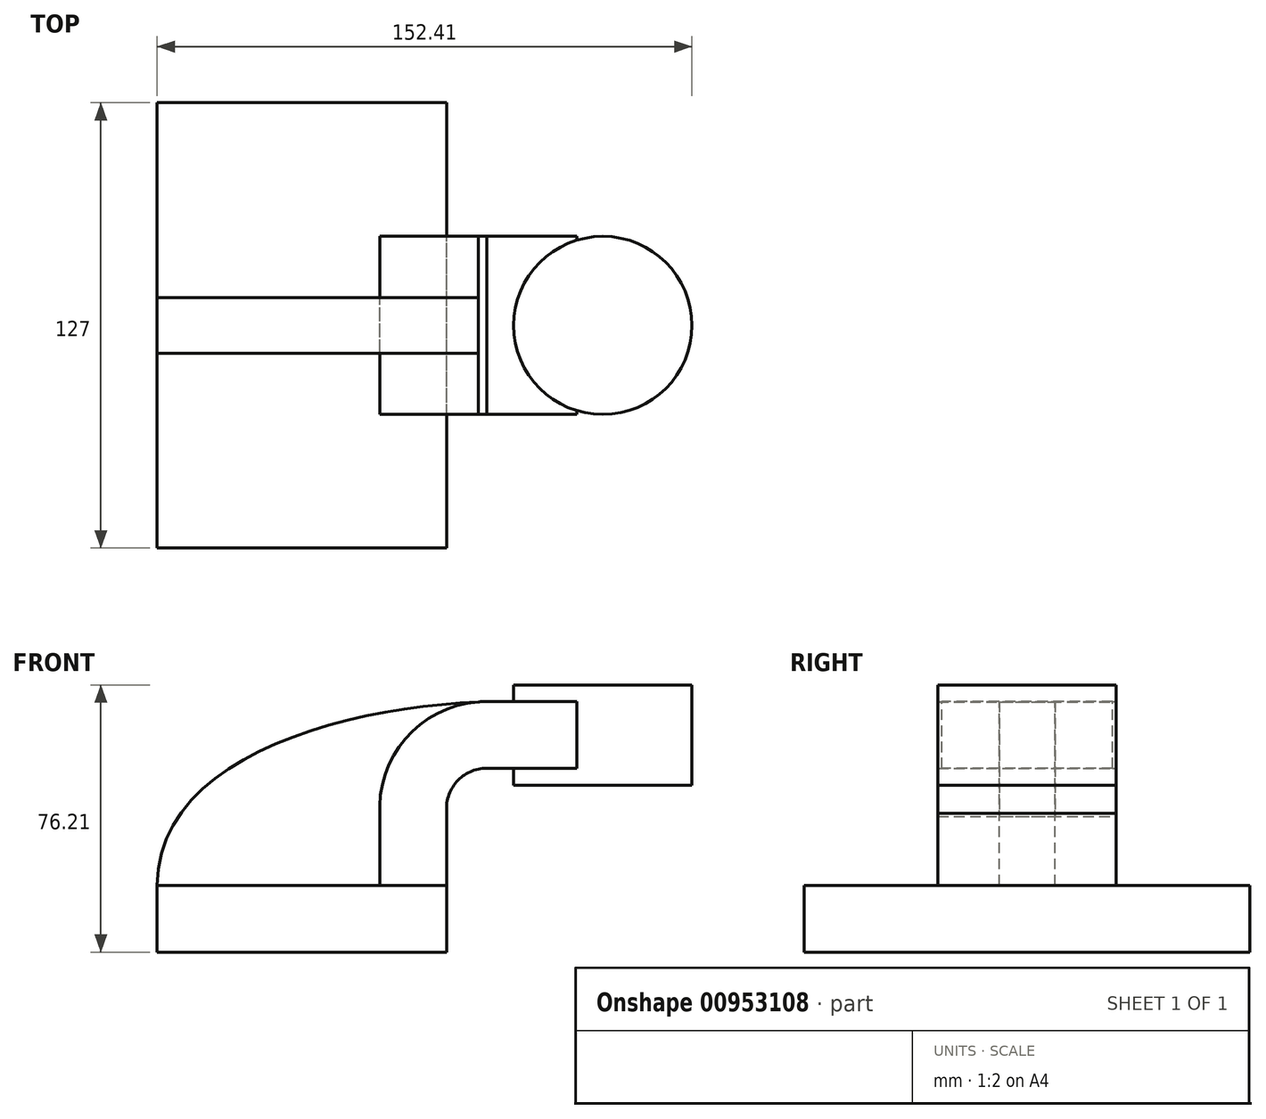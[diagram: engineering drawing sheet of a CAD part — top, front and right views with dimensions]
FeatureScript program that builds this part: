
annotation { "Feature Type Name" : "Feature", "Feature Type Description" : "" }
export const myFeature = defineFeature(function(context is Context, id is Id, definition is map)
    precondition{}
    {
        {
            var Q0;
            Q0=qCreatedBy(makeId("Front.planeOp"),FACE);
            var sketch = newSketch(context, id + "F0", { "sketchPlane" : qUnion([Q0])});
            skLineSegment(sketch, "E0.bottom", {"start": v(-41.28, -9.53) * mm, "end": v(41.28, -9.53) * mm});
            skLineSegment(sketch, "E0.top", {"start": v(-41.28, 9.52) * mm, "end": v(41.28, 9.52) * mm});
            skLineSegment(sketch, "E0.left", {"start": v(-41.28, -9.53) * mm, "end": v(-41.28, 9.53) * mm});
            skLineSegment(sketch, "E0.right", {"start": v(41.28, -9.53) * mm, "end": v(41.28, 9.52) * mm});
            skPoint(sketch, "E0.middle", {"position": v(0, 0) * mm});
            skLineSegment(sketch, "E1.bottom", {"start": v(111.12, 66.67) * mm, "end": v(60.32, 66.67) * mm});
            skLineSegment(sketch, "E1.top", {"start": v(111.12, 38.1) * mm, "end": v(60.32, 38.1) * mm});
            skLineSegment(sketch, "E1.left", {"start": v(111.12, 66.67) * mm, "end": v(111.12, 38.1) * mm});
            skLineSegment(sketch, "E1.right", {"start": v(60.32, 66.67) * mm, "end": v(60.32, 38.1) * mm});
            skPoint(sketch, "E1.middle", {"position": v(85.72, 52.39) * mm});
            skLineSegment(sketch, "E2.bottom", {"start": v(41.28, 9.52) * mm, "end": v(41.28, 9.52) * mm});
            skLineSegment(sketch, "E3", {"start": v(52.62, 42.88) * mm, "end": v(78.31, 42.88) * mm});
            skLineSegment(sketch, "E4", {"start": v(41.28, 9.52) * mm, "end": v(41.28, 30.04) * mm});
            skArc(sketch, "E5", {"start": v(52.62, 42.88) * mm, "mid": v(44.06, 39.01) * mm, "end": v(41.28, 30.04) * mm});
            skLineSegment(sketch, "E6.0", {"start": v(22.23, 9.52) * mm, "end": v(22.23, 29.15) * mm});
            skArc(sketch, "E6.1", {"start": v(52.62, 61.93) * mm, "mid": v(30.27, 52.17) * mm, "end": v(22.23, 29.15) * mm});
            skLineSegment(sketch, "E6.2", {"start": v(52.62, 61.93) * mm, "end": v(78.31, 61.93) * mm});
            skFitSpline(sketch, "E7", {"points": [v(-41.28, 9.53) * mm, v(52.62, 61.93) * mm], "startDerivative": vector(1.16, 112.53) * mm, "endDerivative": vector(116.71, 3.87) * mm});
            skLineSegment(sketch, "E8", {"start": v(78.31, 61.93) * mm, "end": v(78.31, 42.88) * mm});
            skLineSegment(sketch, "E9", {"start": v(85.72, 66.67) * mm, "end": v(85.72, 38.1) * mm});
            skSolve(sketch);
        }
        {
            var Q0;
            Q0=makeQuery(id+"F0.imprint","IMPRINT",FACE,{"disambiguationData":[TD([[makeQuery(id+"F0.imprint","IMPRINT",EDGE,{"derivedFrom":sQuery(id+"F0.wireOp",EDGE,"E0.bottom")}),1.0]])]});
            extrude(context, id + "F1", {"entities" : qUnion([Q0]), "endBound" : BoundingType.SYMMETRIC, "depth" : 127 * mm, "offsetDistance" : 25.4 * mm});
        }
        {
            var Q0;
            {var subQ6=sQuery(id+"F0.wireOp",EDGE,"E4");Q0=makeQuery(id+"F0.imprint","IMPRINT",FACE,{"disambiguationData":[TD([[makeQuery(id+"F0.imprint","IMPRINT",EDGE,{"derivedFrom":subQ6}),1.0]])]});}
            var Q1;
            {var subQ5=sQuery(id+"F0.wireOp",EDGE,"E8");Q1=makeQuery(id+"F0.imprint","IMPRINT",FACE,{"disambiguationData":[TD([[makeQuery(id+"F0.imprint","IMPRINT",EDGE,{"derivedFrom":subQ5}),-1.0]])]});}
            extrude(context, id + "F2", {"entities" : qUnion([Q0, Q1]), "endBound" : BoundingType.SYMMETRIC, "depth" : 50.8 * mm, "offsetDistance" : 25.4 * mm});
        }
        {
            var Q0;
            {var subQ3=sQuery(id+"F0.wireOp",EDGE,"E6.0");Q0=makeQuery(id+"F0.imprint","IMPRINT",FACE,{"disambiguationData":[TD([[makeQuery(id+"F0.imprint","IMPRINT",EDGE,{"derivedFrom":subQ3}),1.0]])]});}
            extrude(context, id + "F3", {"entities" : qUnion([Q0]), "endBound" : BoundingType.SYMMETRIC, "depth" : 15.88 * mm, "offsetDistance" : 25.4 * mm});
        }
        {
            var Q0;
            {var subQ0=sQuery(id+"F0.wireOp",EDGE,"E1.left");Q0=makeQuery(id+"F0.imprint","IMPRINT",FACE,{"disambiguationData":[TD([[makeQuery(id+"F0.imprint","IMPRINT",EDGE,{"derivedFrom":subQ0}),-1.0]])]});}
            var Q1;
            Q1=sQuery(id+"F0.wireOp",EDGE,"E9");
            revolve(context, id + "F4", {"operationType" : NewBodyOperationType.ADD, "surfaceOperationType" : NewSurfaceOperationType.NEW, "entities" : qUnion([Q0]), "axis" : qUnion([Q1]), "revolveType" : RevolveType.FULL});
        }
    });
